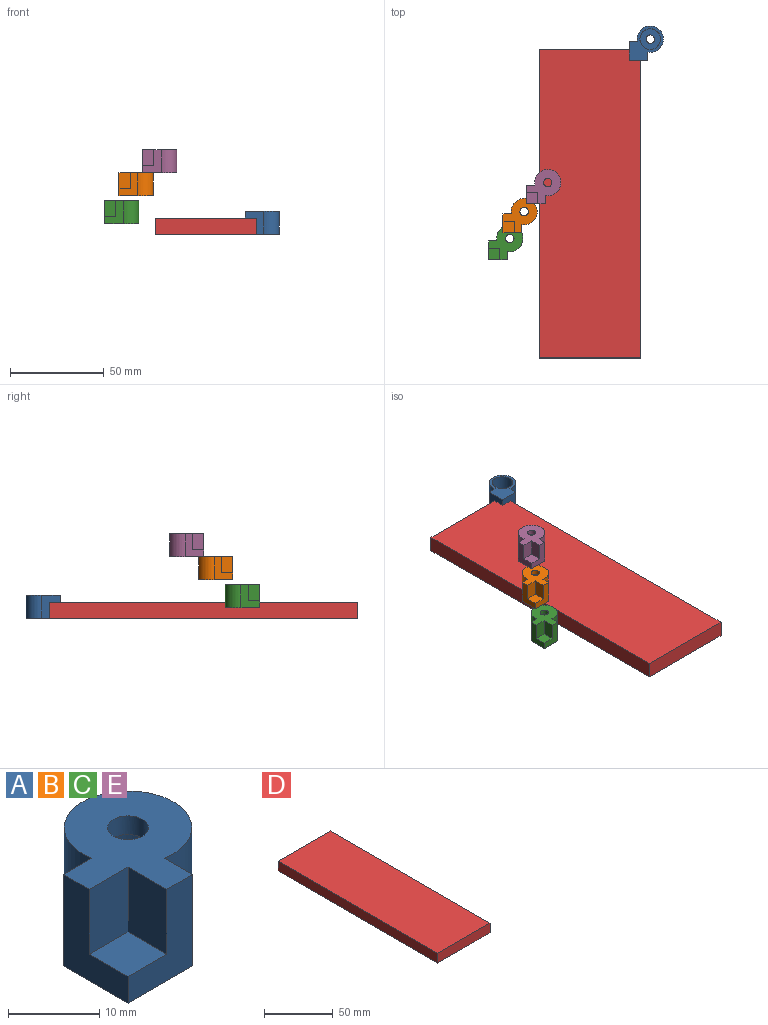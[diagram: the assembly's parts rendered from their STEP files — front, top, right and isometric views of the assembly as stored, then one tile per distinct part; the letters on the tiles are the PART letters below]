
ASSEMBLY  parts=5 mates=1
PART A: 13 faces, bbox 18.3x18.3x12.3 mm
  f0: plane 12.25x10mm, normal (0,-1,0), area 70.3mm2, adj f1,f2,f3,f5,f6,f8
  f1: plane 12.25x10mm, normal (-1,0,0), area 70.3mm2, adj f0,f2,f4,f5,f7,f8
  f2: plane 18.29x18.29mm, normal (0,0,1), area 179.9mm2, adj f0,f1,f3,f4,f6,f7,f9,f12
  f3: plane 12.25x4.41mm, normal (1,0,0), area 54mm2, adj f0,f2,f5,f9
  f4: plane 12.25x4.41mm, normal (0,1,0), area 54mm2, adj f1,f2,f5,f9
  f5: plane 18.29x18.29mm, normal (0,0,-1), area 136.7mm2, adj f0,f1,f3,f4,f9,f11
  f6: plane 8.7x6mm, normal (-1,0,0), area 52.2mm2, adj f0,f2,f7,f8
  f7: plane 8.7x6mm, normal (0,-1,0), area 52.2mm2, adj f1,f2,f6,f8
  f8: plane 6x6mm, normal (0,0,1), area 36mm2, adj f0,f1,f6,f7
  f9: cylinder r=7mm len=14mm, axis (0,0,1), area 435.9mm2, adj f2,f3,f4,f5
  f10: plane 11x11mm, normal (0,0,-1), area 79.1mm2, adj f11,f12
  f11: cylinder r=5.5mm len=11mm, axis (0,0,-1), area 336.9mm2, adj f5,f10
  f12: cylinder r=2.25mm len=4.5mm, axis (0,0,-1), area 35.3mm2, adj f2,f10
PART B: same geometry as A
PART C: same geometry as A
PART D: 6 faces, bbox 54x164.8x8.7 mm
  f0: plane 164.8x8.7mm, normal (1,0,0), area 1433.8mm2, adj f1,f3,f4,f5
  f1: plane 54x8.7mm, normal (0,1,0), area 469.8mm2, adj f0,f2,f4,f5
  f2: plane 164.8x8.7mm, normal (-1,0,0), area 1433.8mm2, adj f1,f3,f4,f5
  f3: plane 54x8.7mm, normal (0,-1,0), area 469.8mm2, adj f0,f2,f4,f5
  f4: plane 164.8x54mm, normal (0,0,1), area 8899.2mm2, adj f0,f1,f2,f3
  f5: plane 164.8x54mm, normal (0,0,-1), area 8899.2mm2, adj f0,f1,f2,f3
PART E: same geometry as A
PLACE A rot(axis=(0.71,0.71,0),180deg) t=(20.5,80.5,12.57)mm
PLACE B t=(-46.76,-11.52,20.99)mm
PLACE C t=(-54.42,-25.88,6.07)mm
PLACE D t=(-3.5,1.1,0.32)mm
PLACE E t=(-34.17,3.91,33.22)mm
MATE fastened A.f8 <-> D.f4  axis (0,0,-1) through (20.5,80.5,9.02)mm
